# Revit family: Building-IEC309Connections-GEWISS-IEC309HP-10°_FLUSH-MOUNT_SOCKET_FRENCH_STD
name_source: partatom
category: Apparecchi elettrici
units: mm (PartAtom-declared; Revit-internal decimal feet)

## family parameters
Condiviso = No
Host = Superficie
Mantenere orientamento annotazione = Sì
Punto di calcolo locali = Sì
Quota connettore circolare = Usa diametro
Taglio con vuoti quando caricato = No
Tipo di parte = Normale

## types (1)
- GW62394 - FRANCE IP54 S.O. WITH FLANGE
    BLOCCO = B=C
    Catalogue = BUILDING
    Colour: = Blue
    Corpo centrale = Default(2)
    Descrizione = FRANCE IP54 S.O. WITH FLANGE
    FORMULA = 1000 mm  [stored 3.28084 ft]
    Flange dimensions (mm) = 50x50
    Frequency = 50/60 Hz
    Glow wire test: = 850 °C (active parts) - 650 °C (passive parts)
    IDF = 65b9bbc2-6d20-4e3d-b48d-4849ab76a026
    IDT = 352582b9d6f34e52b9ed5e1fa65b8919
    IP degree = IP54
    Immagine tipo = <Nessuno>
    L = 155 mm
    Modello = GW62394
    No. of poles = 2P+E
    Operating temperature: = -25 +55 °C
    Piastra = Default(2)
    Produttore = GEWISS S.p.A.
    Prospetto di default = 500 mm
    Rated current (A) = 16
    Rated voltage = 230V
    SEO = Socket outlet
    SPinotto = Default(2)
    Sportello_visibile = Sì
    Spostamento_S = 957 mm
    Standard: = French
    Technical sheet = https://www.gewiss.com
    Thermo-pressure with ball = 125 °C (active parts) - 80 °C (passive parts)
    Type of wiring = With screw
    URL = https://www.gewiss.com
    Version file RFA = 21.11
    W = 115 mm

note: [stored X ft] marks values corroborated as IEEE doubles in the binary element streams (Revit-internal decimal feet)

## geometry (parser evidence)
native form markers: Sweep x2
no freeform markers — native parametric forms only
